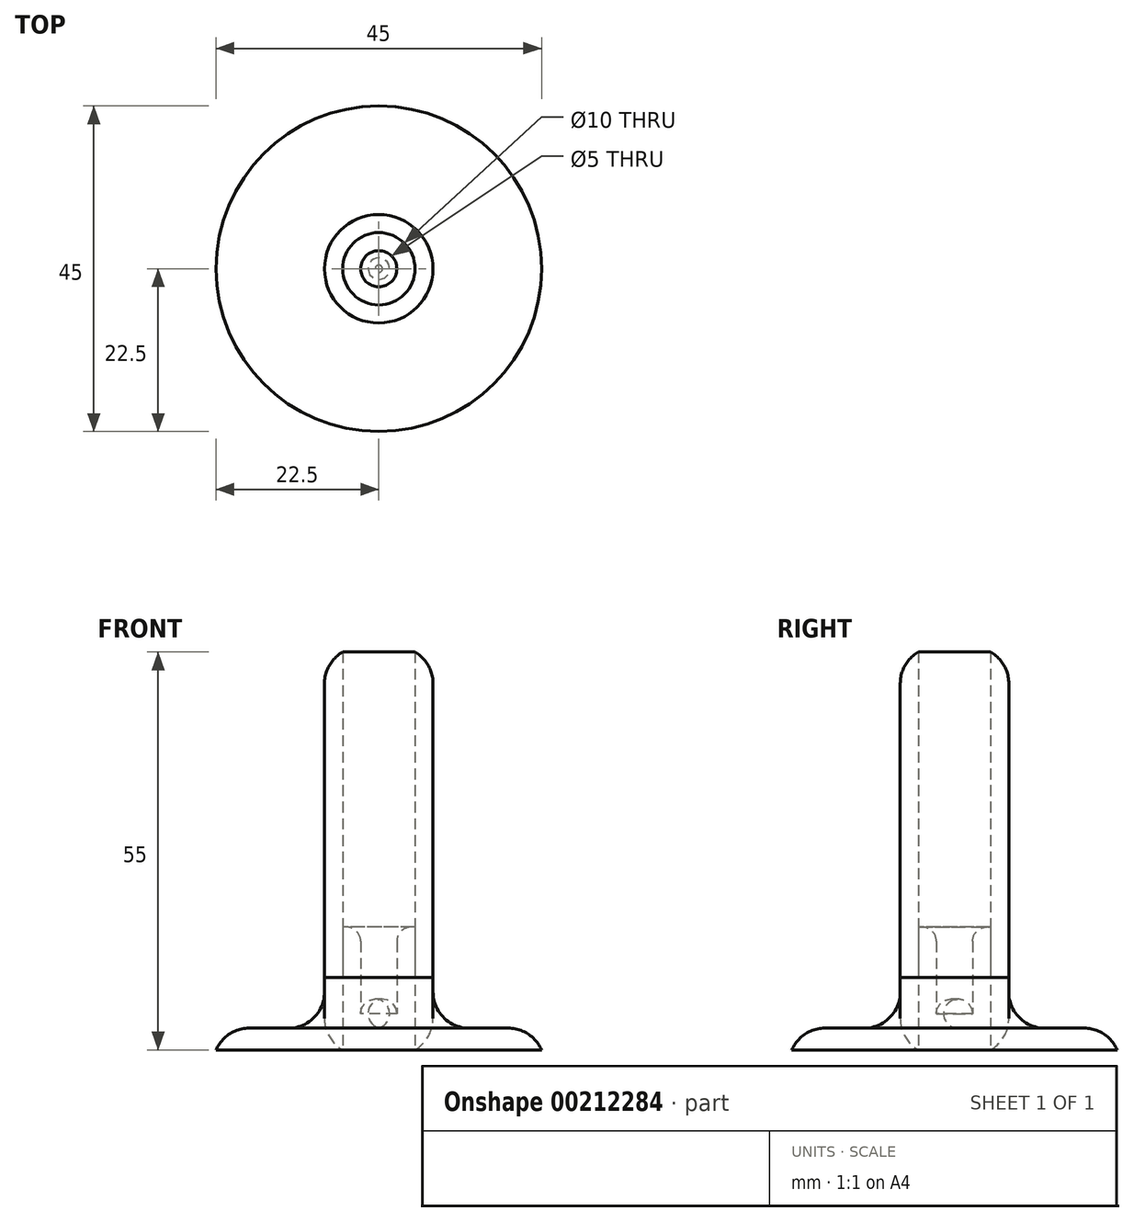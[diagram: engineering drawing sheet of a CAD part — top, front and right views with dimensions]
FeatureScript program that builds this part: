
annotation { "Feature Type Name" : "Feature", "Feature Type Description" : "" }
export const myFeature = defineFeature(function(context is Context, id is Id, definition is map)
    precondition{}
    {
        {
            var Q0;
            Q0=qCreatedBy(makeId("Top.planeOp"),FACE);
            var sketch = newSketch(context, id + "F0", { "sketchPlane" : qUnion([Q0])});
            skCircle(sketch, "E0", {"center": v(0, 0) * mm, "radius": 5 * mm});
            skCircle(sketch, "E1", {"center": v(0, 0) * mm, "radius": 22.5 * mm});
            skCircle(sketch, "E2", {"center": v(0, 0) * mm, "radius": 2.5 * mm});
            skCircle(sketch, "E3", {"center": v(0, 0) * mm, "radius": 7.5 * mm});
            skSolve(sketch);
        }
        {
            var Q0;
            Q0 = qSketchRegion(id + "F0", true);
            var Q1;
            Q1=makeQuery(id+"F0.imprint","IMPRINT",FACE,{"disambiguationData":[TD([[makeQuery(id+"F0.imprint","IMPRINT",EDGE,{"derivedFrom":sQuery(id+"F0.wireOp",EDGE,"E0")}),1.0]])]});
            var Q2;
            Q2=makeQuery(id+"F0.imprint","IMPRINT",FACE,{"disambiguationData":[TD([[makeQuery(id+"F0.imprint","IMPRINT",EDGE,{"derivedFrom":sQuery(id+"F0.wireOp",EDGE,"E2")}),1.0]])]});
            var Q3;
            Q3=makeQuery(id+"F0.imprint","IMPRINT",FACE,{"disambiguationData":[TD([[makeQuery(id+"F0.imprint","IMPRINT",EDGE,{"derivedFrom":sQuery(id+"F0.wireOp",EDGE,"E0")}),-1.0]])]});
            extrude(context, id + "F1", {"entities" : qUnion([Q0, Q1, Q2, Q3]), "depth" : 3 * mm});
        }
        {
            var Q0;
            Q0=makeQuery(id+"F0.imprint","IMPRINT",FACE,{"disambiguationData":[TD([[makeQuery(id+"F0.imprint","IMPRINT",EDGE,{"derivedFrom":sQuery(id+"F0.wireOp",EDGE,"E0")}),1.0]])]});
            extrude(context, id + "F2", {"entities" : qUnion([Q0]), "depth" : 17 * mm});
        }
        {
            var Q0;
            Q0=makeQuery(id+"F0.imprint","IMPRINT",FACE,{"disambiguationData":[TD([[makeQuery(id+"F0.imprint","IMPRINT",EDGE,{"derivedFrom":sQuery(id+"F0.wireOp",EDGE,"E0")}),-1.0]])]});
            extrude(context, id + "F3", {"entities" : qUnion([Q0]), "operationType" : NewBodyOperationType.ADD, "depth" : 10 * mm});
        }
        {
            var Q0;
            {var subQ0=sQuery(id+"F0.wireOp",EDGE,"E1");Q0=makeQuery(id+"F3.boolean.opBoolean","SPLIT",FACE,{"disambiguationData":[TD([makeQuery(id+"F1.opExtrude","SWEPT_FACE",FACE,{"disambiguationData":[OSD([subQ0])]})])],"derivedFrom":makeQuery(id+"F1.opExtrude","CAP_FACE",FACE,{"disambiguationData":[OSD([subQ0])],"isStart":false})});}
            fillet(context, id + "F4", {"entities" : qUnion([Q0]), "radius" : 5 * mm, "tangentPropagation" : true, "allowEdgeOverflow" : false});
        }
        {
            var Q0;
            Q0=makeQuery(id+"F0.imprint","IMPRINT",FACE,{"disambiguationData":[TD([[makeQuery(id+"F0.imprint","IMPRINT",EDGE,{"derivedFrom":sQuery(id+"F0.wireOp",EDGE,"E0")}),-1.0]])]});
            extrude(context, id + "F5", {"entities" : qUnion([Q0]), "depth" : 55 * mm});
        }
        {
            var Q0;
            Q0=makeQuery(id+"F5.opExtrude","SWEPT_FACE",FACE,{"disambiguationData":[OSD([sQuery(id+"F0.wireOp",EDGE,"E3")])]});
            fillet(context, id + "F6", {"entities" : qUnion([Q0]), "radius" : 5 * mm, "tangentPropagation" : true, "allowEdgeOverflow" : false});
        }
        {
            var Q0;
            Q0=makeQuery(id+"F2.opExtrude","SWEPT_FACE",FACE,{"disambiguationData":[OSD([sQuery(id+"F0.wireOp",EDGE,"E2")])]});
            fillet(context, id + "F7", {"entities" : qUnion([Q0]), "radius" : 2 * mm, "tangentPropagation" : true, "allowEdgeOverflow" : false});
        }
    });
